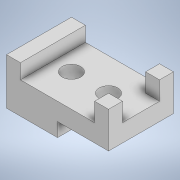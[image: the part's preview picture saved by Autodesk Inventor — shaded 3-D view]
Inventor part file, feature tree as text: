
AUTODESK INVENTOR PART (.ipt)
format: ipt  version: 2022 (Build 260153000, 153)  size: 134,144 bytes
history: native  units: mm
features: extrude x3, sketch x2, other x1
ambient origin geometry x8: Origin, YZ Plane, XZ Plane, XY Plane, X Axis, Y Axis, Z Axis, Center Point
bodies: Body1 (feature_tree)
feature tree (6):
  other  "Sólido1"
  extrude  "Extrusão1"  Depth=50.0mm
  sketch  "Esboço4"  dims[d2=15.0mm d3=16.0mm d7=15.0mm d8=55.0mm d9=95.0mm d10=70.0mm d11=0.0mm d19=20.0mm d20=20.0mm d21=20.0mm d22=40.0mm d23=35.0mm d24=15.0mm d25=15.0mm d26=15.0mm d27=15.0mm d28=0.0mm d29=0.0mm d30=20.0mm d31=0.0mm d12=0.872665mm]
  extrude  "Extrusão3"  Depth=16.0mm
  extrude  "Extrusão4"  Depth=15.0mm
  sketch  "Esboço1"  dims[d0=55.0mm d1=50.0mm]
